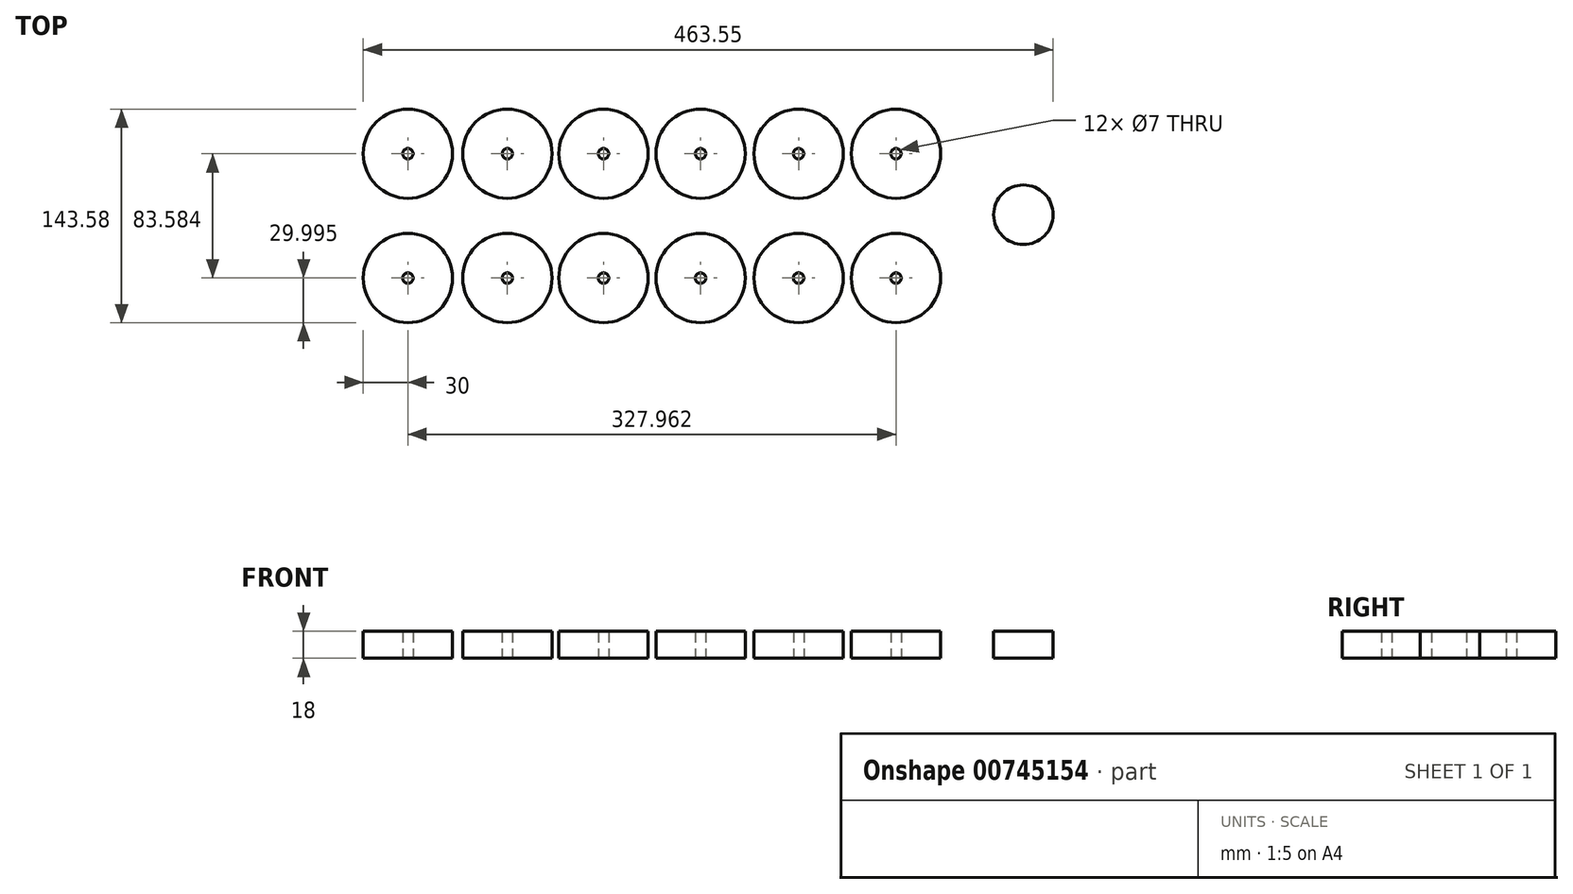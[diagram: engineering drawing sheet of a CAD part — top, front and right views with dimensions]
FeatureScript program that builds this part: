
annotation { "Feature Type Name" : "Feature", "Feature Type Description" : "" }
export const myFeature = defineFeature(function(context is Context, id is Id, definition is map)
    precondition{}
    {
        {
            var Q0;
            Q0=qCreatedBy(makeId("Top.planeOp"),FACE);
            var sketch = newSketch(context, id + "F0", { "sketchPlane" : qUnion([Q0])});
            skLineSegment(sketch, "E0.bottom", {"start": v(-250.17, 91.25) * mm, "end": v(249.83, 91.25) * mm, "construction": true});
            skLineSegment(sketch, "E0.top", {"start": v(-250.17, -108.75) * mm, "end": v(249.83, -108.75) * mm, "construction": true});
            skLineSegment(sketch, "E0.left", {"start": v(-250.17, 91.25) * mm, "end": v(-250.17, -108.75) * mm, "construction": true});
            skLineSegment(sketch, "E0.right", {"start": v(249.83, 91.25) * mm, "end": v(249.83, -108.75) * mm, "construction": true});
            skCircle(sketch, "E1", {"center": v(-211.35, 50.7) * mm, "radius": 30 * mm});
            skLineSegment(sketch, "E2", {"start": v(-250.17, 50.7) * mm, "end": v(249.83, 50.7) * mm, "construction": true});
            skCircle(sketch, "E3", {"center": v(-144.5, 50.7) * mm, "radius": 30 * mm});
            skCircle(sketch, "E4", {"center": v(-79.91, 50.7) * mm, "radius": 30 * mm});
            skCircle(sketch, "E5", {"center": v(-14.68, 50.7) * mm, "radius": 30 * mm});
            skCircle(sketch, "E6", {"center": v(51.16, 50.7) * mm, "radius": 30 * mm});
            skCircle(sketch, "E7", {"center": v(116.61, 50.7) * mm, "radius": 30 * mm});
            skCircle(sketch, "E8", {"center": v(-211.35, -32.88) * mm, "radius": 30 * mm});
            skLineSegment(sketch, "E9", {"start": v(-250.17, -32.88) * mm, "end": v(249.83, -32.88) * mm, "construction": true});
            skCircle(sketch, "E10", {"center": v(-144.5, -32.88) * mm, "radius": 30 * mm});
            skCircle(sketch, "E11", {"center": v(-79.91, -32.88) * mm, "radius": 30 * mm});
            skCircle(sketch, "E12", {"center": v(-14.68, -32.88) * mm, "radius": 30 * mm});
            skCircle(sketch, "E13", {"center": v(51.16, -32.88) * mm, "radius": 30 * mm});
            skCircle(sketch, "E14", {"center": v(116.61, -32.88) * mm, "radius": 30 * mm});
            skCircle(sketch, "E15", {"center": v(-211.35, 50.7) * mm, "radius": 3.5 * mm});
            skCircle(sketch, "E16", {"center": v(-144.5, 50.7) * mm, "radius": 3.5 * mm});
            skCircle(sketch, "E17", {"center": v(-79.91, 50.7) * mm, "radius": 3.5 * mm});
            skCircle(sketch, "E18", {"center": v(-14.68, 50.7) * mm, "radius": 3.5 * mm});
            skCircle(sketch, "E19", {"center": v(51.16, 50.7) * mm, "radius": 3.5 * mm});
            skCircle(sketch, "E20", {"center": v(116.61, 50.7) * mm, "radius": 3.5 * mm});
            skCircle(sketch, "E21", {"center": v(-211.35, -32.88) * mm, "radius": 3.5 * mm});
            skCircle(sketch, "E22", {"center": v(-144.5, -32.88) * mm, "radius": 3.5 * mm});
            skCircle(sketch, "E23", {"center": v(-79.91, -32.88) * mm, "radius": 3.5 * mm});
            skCircle(sketch, "E24", {"center": v(-14.68, -32.88) * mm, "radius": 3.5 * mm});
            skCircle(sketch, "E25", {"center": v(51.16, -32.88) * mm, "radius": 3.5 * mm});
            skCircle(sketch, "E26", {"center": v(116.61, -32.88) * mm, "radius": 3.5 * mm});
            skCircle(sketch, "E27", {"center": v(202.2, 9.66) * mm, "radius": 20 * mm});
            skSolve(sketch);
        }
        {
            var Q0;
            Q0 = qSketchRegion(id + "F0", true);
            extrude(context, id + "F1", {"entities" : qUnion([Q0]), "depth" : 18 * mm, "offsetDistance" : 25 * mm});
        }
    });
